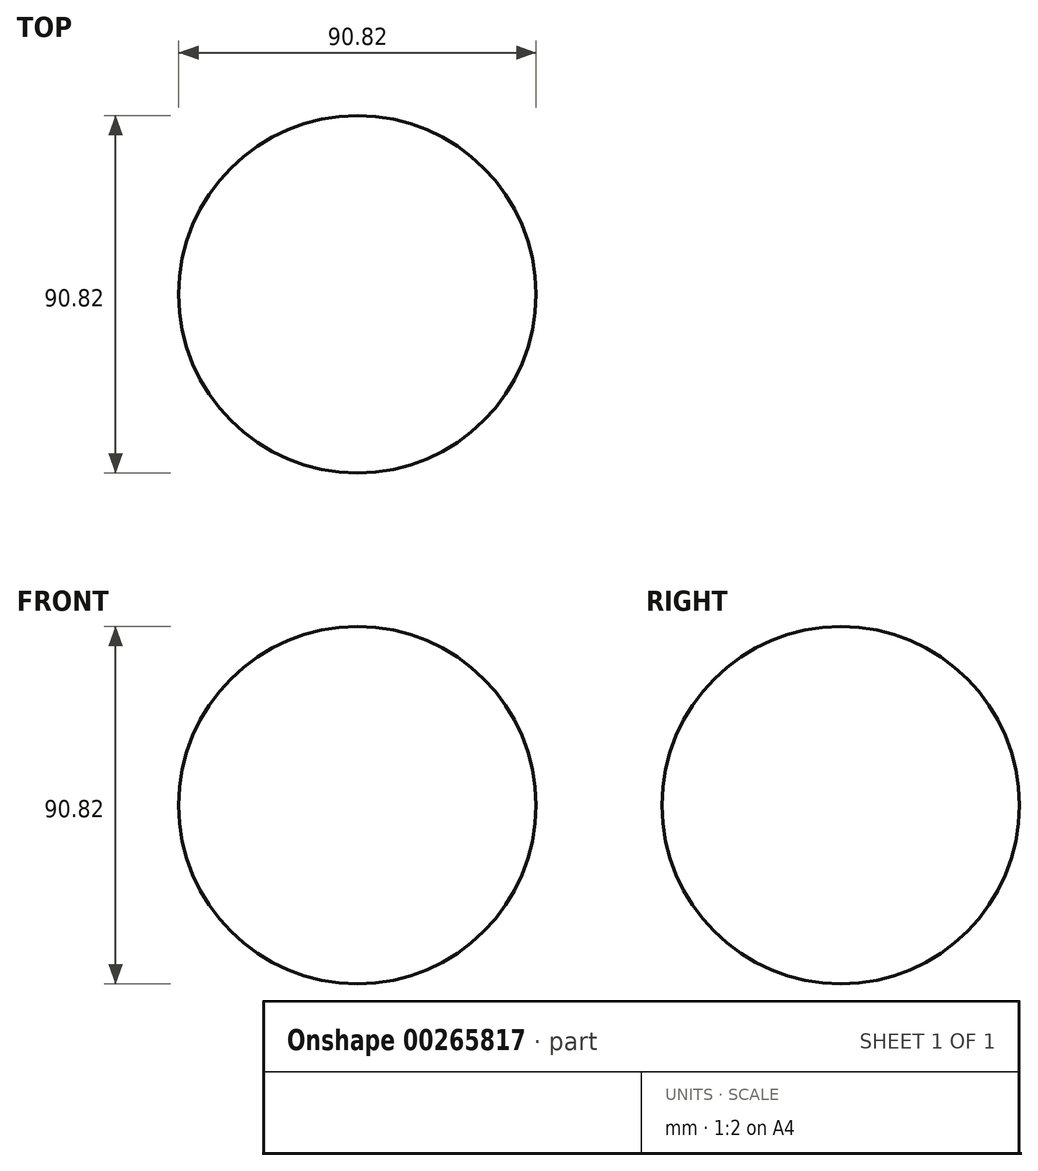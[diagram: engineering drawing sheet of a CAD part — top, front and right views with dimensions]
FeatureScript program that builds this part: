
annotation { "Feature Type Name" : "Feature", "Feature Type Description" : "" }
export const myFeature = defineFeature(function(context is Context, id is Id, definition is map)
    precondition{}
    {
        {
            var Q0;
            Q0=qCreatedBy(makeId("Top.planeOp"),FACE);
            var sketch = newSketch(context, id + "F0", { "sketchPlane" : qUnion([Q0])});
            skArc(sketch, "E0", {"start": v(45.4, 0) * mm, "mid": v(0, 45.4) * mm, "end": v(-45.4, 0) * mm});
            skLineSegment(sketch, "E1", {"start": v(-45.4, 0) * mm, "end": v(45.4, 0) * mm});
            skSolve(sketch);
        }
        {
            var Q0;
            Q0=makeQuery(id+"F0.imprint","IMPRINT",FACE,{"disambiguationData":[TD([[makeQuery(id+"F0.imprint","IMPRINT",EDGE,{"derivedFrom":sQuery(id+"F0.wireOp",EDGE,"E0")}),1.0]])]});
            var Q1;
            Q1=sQuery(id+"F0.wireOp",EDGE,"E1");
            revolve(context, id + "F1", {"entities" : qUnion([Q0]), "axis" : qUnion([Q1]), "revolveType" : RevolveType.FULL});
        }
    });
